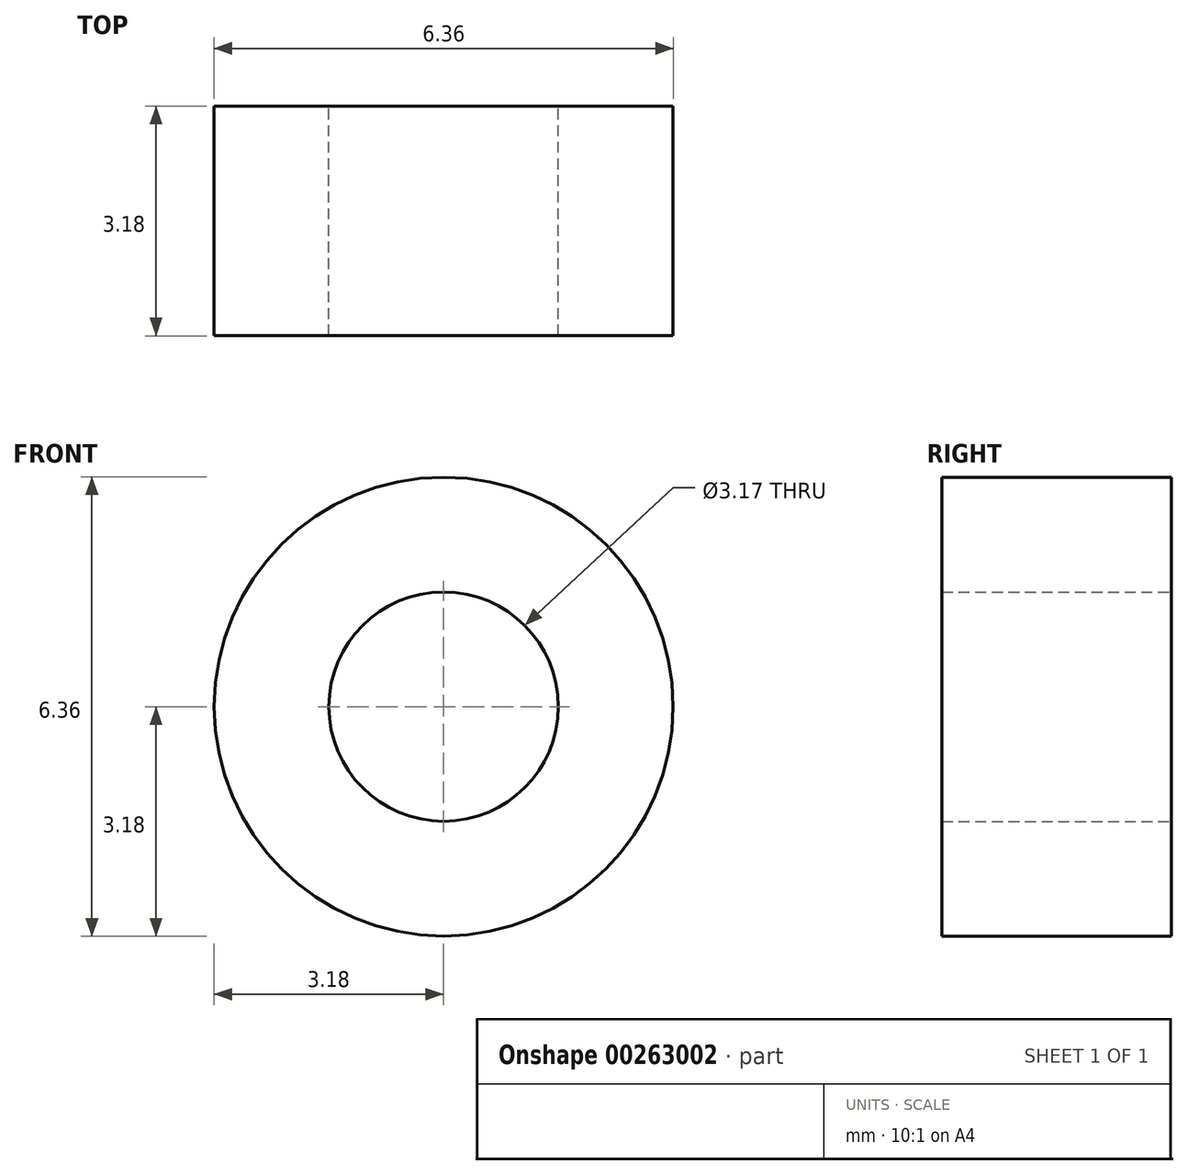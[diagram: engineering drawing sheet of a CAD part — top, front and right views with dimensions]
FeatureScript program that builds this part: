
annotation { "Feature Type Name" : "Feature", "Feature Type Description" : "" }
export const myFeature = defineFeature(function(context is Context, id is Id, definition is map)
    precondition{}
    {
        {
            var Q0;
            Q0=qCreatedBy(makeId("Front.planeOp"),FACE);
            var sketch = newSketch(context, id + "F0", { "sketchPlane" : qUnion([Q0])});
            skCircle(sketch, "E0", {"center": v(0, 0) * mm, "radius": 3.18 * mm});
            skCircle(sketch, "E1", {"center": v(0, 0) * mm, "radius": 1.59 * mm});
            skSolve(sketch);
        }
        {
            var Q0;
            Q0=makeQuery(id+"F0.imprint","IMPRINT",FACE,{"disambiguationData":[TD([[makeQuery(id+"F0.imprint","IMPRINT",EDGE,{"derivedFrom":sQuery(id+"F0.wireOp",EDGE,"E0")}),1.0]])]});
            extrude(context, id + "F1", {"entities" : qUnion([Q0]), "depth" : 3.17 * mm});
        }
    });
